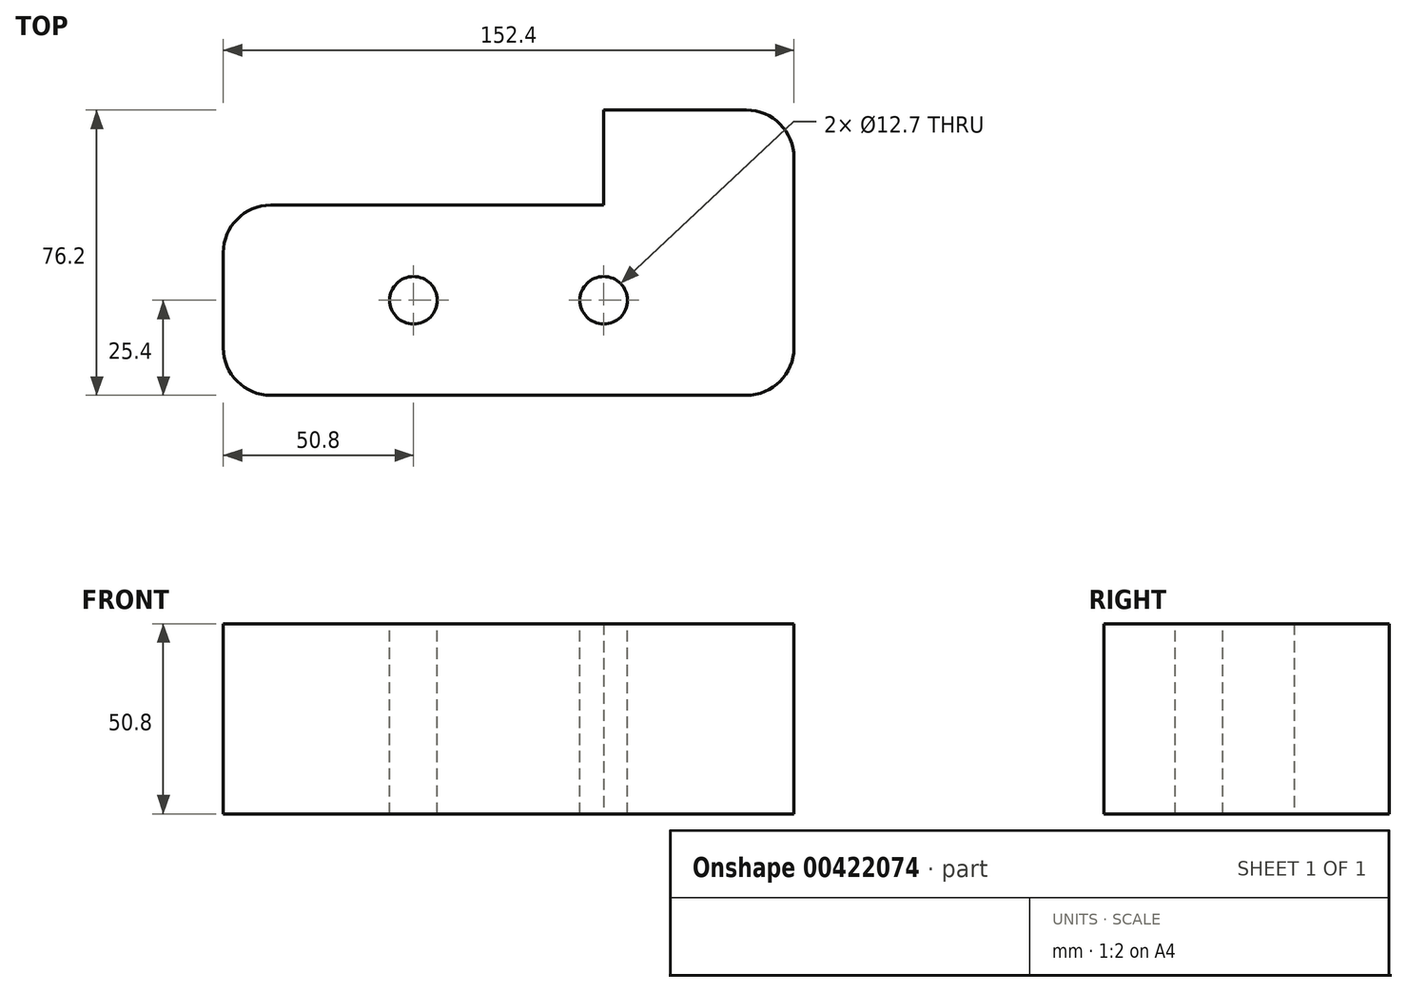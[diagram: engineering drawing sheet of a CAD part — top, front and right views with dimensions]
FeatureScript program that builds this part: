
annotation { "Feature Type Name" : "Feature", "Feature Type Description" : "" }
export const myFeature = defineFeature(function(context is Context, id is Id, definition is map)
    precondition{}
    {
        {
            var Q0;
            Q0=qCreatedBy(makeId("Top.planeOp"),FACE);
            var sketch = newSketch(context, id + "F0", { "sketchPlane" : qUnion([Q0])});
            skLineSegment(sketch, "E0", {"start": v(0, 0) * mm, "end": v(152.4, 0) * mm});
            skLineSegment(sketch, "E1", {"start": v(0, 0) * mm, "end": v(0, 50.8) * mm});
            skLineSegment(sketch, "E2", {"start": v(0, 50.8) * mm, "end": v(101.6, 50.8) * mm});
            skLineSegment(sketch, "E3", {"start": v(101.6, 50.8) * mm, "end": v(101.6, 76.2) * mm});
            skLineSegment(sketch, "E4", {"start": v(101.6, 76.2) * mm, "end": v(152.4, 76.2) * mm});
            skLineSegment(sketch, "E5", {"start": v(152.4, 0) * mm, "end": v(152.4, 76.2) * mm});
            skSolve(sketch);
        }
        {
            var Q0;
            Q0 = qSketchRegion(id + "F0", true);
            extrude(context, id + "F1", {"entities" : qUnion([Q0]), "depth" : 50.8 * mm});
        }
        {
            var Q0;
            Q0=makeQuery(id+"F1.opExtrude","SWEPT_EDGE",EDGE,{"disambiguationData":[OSD([sQuery(id+"F0.wireOp",EDGE,"E4"),sQuery(id+"F0.wireOp",EDGE,"E5")])]});
            var Q1;
            Q1=makeQuery(id+"F1.opExtrude","SWEPT_EDGE",EDGE,{"disambiguationData":[OSD([sQuery(id+"F0.wireOp",EDGE,"E0"),sQuery(id+"F0.wireOp",EDGE,"E5")])]});
            var Q2;
            Q2=makeQuery(id+"F1.opExtrude","SWEPT_EDGE",EDGE,{"disambiguationData":[OSD([sQuery(id+"F0.wireOp",EDGE,"E0"),sQuery(id+"F0.wireOp",EDGE,"E1")])]});
            var Q3;
            Q3=makeQuery(id+"F1.opExtrude","SWEPT_EDGE",EDGE,{"disambiguationData":[OSD([sQuery(id+"F0.wireOp",EDGE,"E1"),sQuery(id+"F0.wireOp",EDGE,"E2")])]});
            fillet(context, id + "F2", {"entities" : qUnion([Q0, Q1, Q2, Q3]), "radius" : 12.7 * mm, "tangentPropagation" : true, "allowEdgeOverflow" : false});
        }
        {
            var Q0;
            Q0=makeQuery(id+"F1.opExtrude","CAP_FACE",FACE,{"disambiguationData":[OSD([sQuery(id+"F0.wireOp",EDGE,"E0"),sQuery(id+"F0.wireOp",EDGE,"E1"),sQuery(id+"F0.wireOp",EDGE,"E2"),sQuery(id+"F0.wireOp",EDGE,"E3"),sQuery(id+"F0.wireOp",EDGE,"E4"),sQuery(id+"F0.wireOp",EDGE,"E5")])],"isStart":false});
            var sketch = newSketch(context, id + "F3", { "sketchPlane" : qUnion([Q0])});
            skPoint(sketch, "E6", {"position": v(50.8, 25.4) * mm});
            skPoint(sketch, "E6.positionSnap0", {"position": v(0, 25.4) * mm});
            skPoint(sketch, "E7", {"position": v(101.6, 25.4) * mm});
            skSolve(sketch);
        }
        {
            var Q0;
            Q0=sQuery(id+"F3.wireOp",VERTEX,"E6");
            var Q1;
            Q1=sQuery(id+"F3.wireOp",VERTEX,"E7");
            var Q2;
            Q2=makeQuery(id+"F1.opExtrude","SWEPT_BODY",BODY,{"disambiguationData":[OSD([sQuery(id+"F0.wireOp",EDGE,"E0"),sQuery(id+"F0.wireOp",EDGE,"E1"),sQuery(id+"F0.wireOp",EDGE,"E2"),sQuery(id+"F0.wireOp",EDGE,"E3"),sQuery(id+"F0.wireOp",EDGE,"E4"),sQuery(id+"F0.wireOp",EDGE,"E5")])]});
            hole(context, id + "F4", {"style" : HoleStyle.SIMPLE, "endStyle" : HoleEndStyle.THROUGH, "holeDiameter" : 12.7 * mm, "isTappedThrough" : true, "tappedDepth" : 12.7 * mm, "tapClearance" : 3, "locations" : qUnion([Q0, Q1]), "scope" : qUnion([Q2])});
        }
    });
